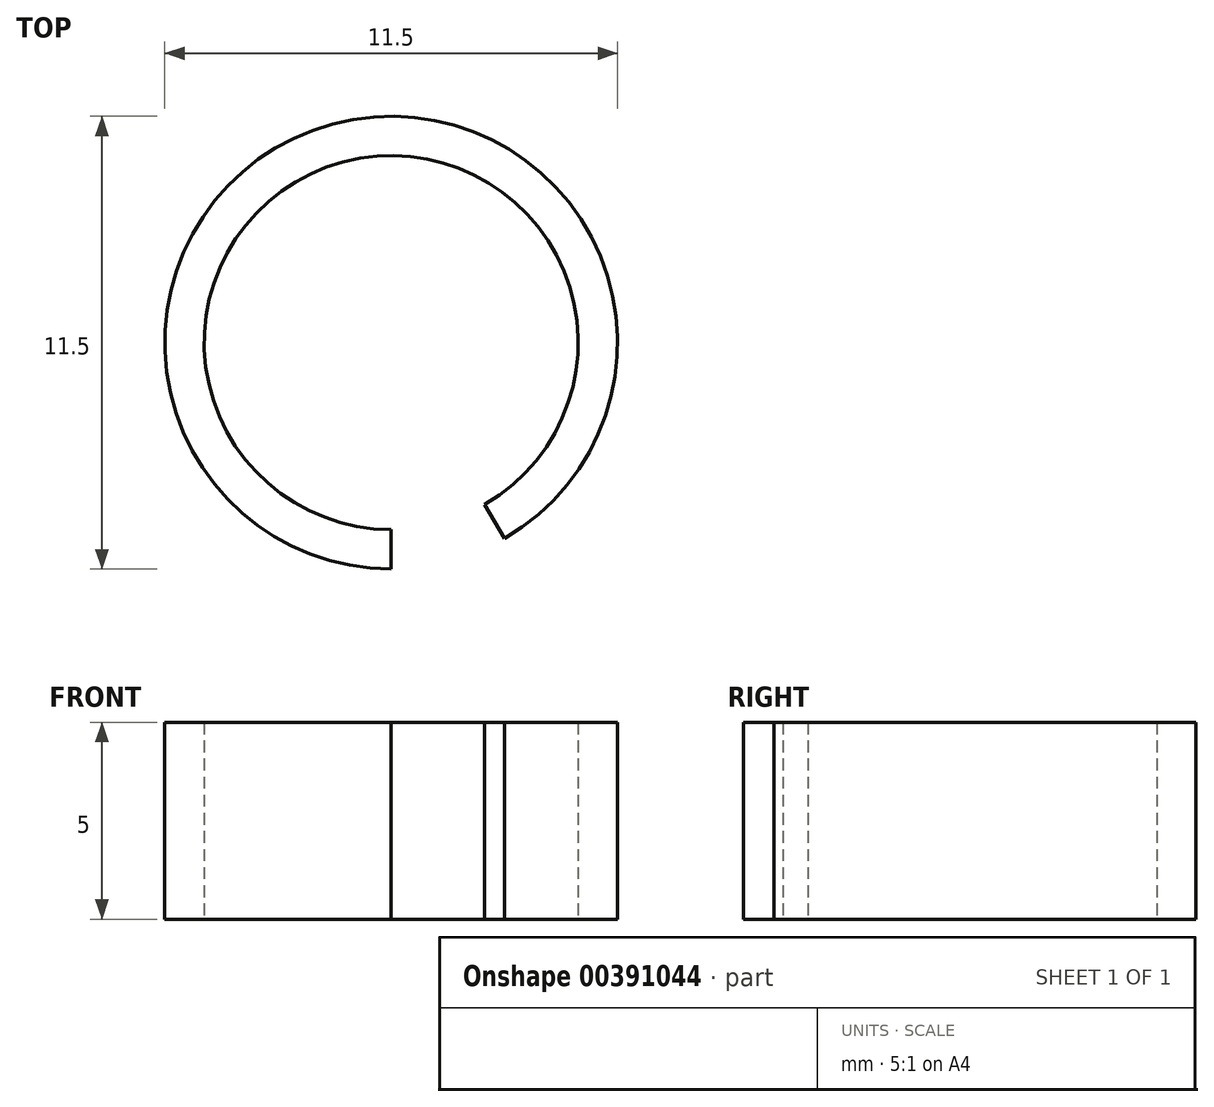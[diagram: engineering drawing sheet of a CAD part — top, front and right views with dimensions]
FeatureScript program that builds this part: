
annotation { "Feature Type Name" : "Feature", "Feature Type Description" : "" }
export const myFeature = defineFeature(function(context is Context, id is Id, definition is map)
    precondition{}
    {
        {
            var Q0;
            Q0=qCreatedBy(makeId("Top.planeOp"),FACE);
            var sketch = newSketch(context, id + "F0", { "sketchPlane" : qUnion([Q0])});
            skArc(sketch, "E0", {"start": v(2.38, -4.11) * mm, "mid": v(-1.23, 4.59) * mm, "end": v(0, -4.75) * mm});
            skArc(sketch, "E1", {"start": v(2.88, -4.98) * mm, "mid": v(-1.49, 5.55) * mm, "end": v(0, -5.75) * mm});
            skLineSegment(sketch, "E2", {"start": v(2.38, -4.11) * mm, "end": v(2.38, -4.11) * mm});
            skLineSegment(sketch, "E3", {"start": v(0, -4.75) * mm, "end": v(0, -5.75) * mm});
            skLineSegment(sketch, "E4", {"start": v(2.38, -4.11) * mm, "end": v(2.88, -4.98) * mm});
            skSolve(sketch);
        }
        {
            var Q0;
            Q0=makeQuery(id+"F0.imprint","IMPRINT",FACE,{"disambiguationData":[TD([[makeQuery(id+"F0.imprint","IMPRINT",EDGE,{"derivedFrom":sQuery(id+"F0.wireOp",EDGE,"E0")}),-1.0]])]});
            extrude(context, id + "F1", {"entities" : qUnion([Q0]), "depth" : 5 * mm});
        }
    });
